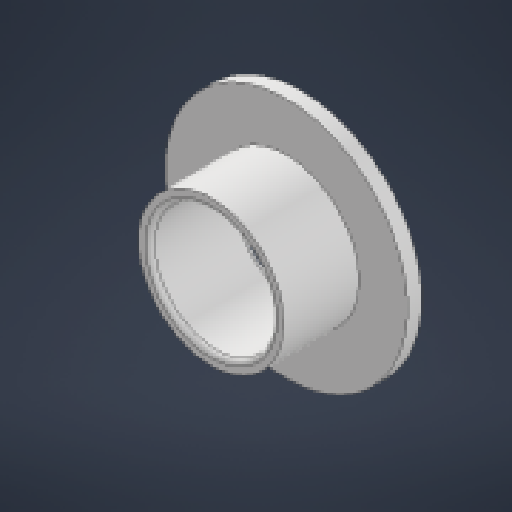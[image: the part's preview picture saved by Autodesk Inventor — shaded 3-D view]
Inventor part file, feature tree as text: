
AUTODESK INVENTOR PART (.ipt)
format: ipt  version: 2024.1 (Build 281209000, 209)  size: 167,424 bytes
history: native  units: in
note: dims shown in document units (in); Inventor stores cm internally (conversion verified against a paired STEP export)
features: other x4, extrude x2, sketch x2, reference x2, fillet x1
ambient origin geometry x8: Origin, YZ Plane, XZ Plane, XY Plane, X Axis, Y Axis, Z Axis, Center Point
bodies: Solid1 (feature_tree)
feature tree (11):
  extrude  "Extrusion1"  Depth=0.005in
  fillet  "Fillet1"  Radius=0.0925in
  extrude  "Extrusion2"  Depth=0.015in
  sketch  "Sketch1"  dims[d0=0.003in d1=0.005in d2=0.0925in d3=0.0in]
  reference  "Reference1"
  reference  "Reference2"
  sketch  "Sketch2"  dims[d4=0.005in d5=0.25in d6=0.015in d7=0.0in]
  other  "<userpath>\Documents\School\FallCAD\Bio\Bio.iam"
  other  "Bio.iam"
  other  "ServoMount:1"
  other  "FrontLinkage:1"
